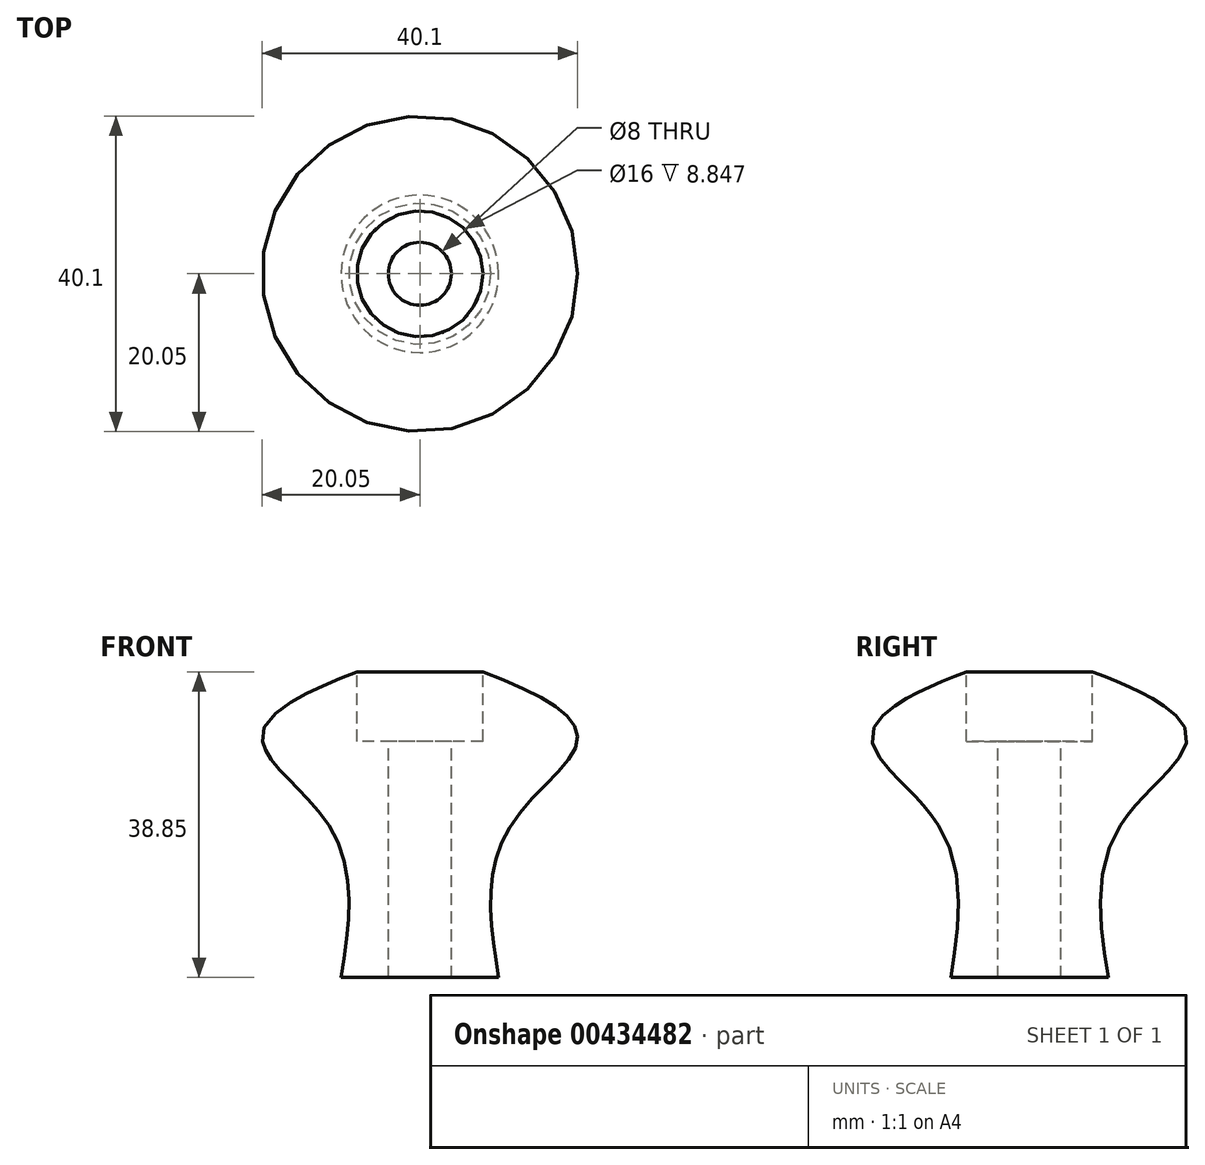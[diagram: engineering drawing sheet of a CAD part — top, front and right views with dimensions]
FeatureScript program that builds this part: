
annotation { "Feature Type Name" : "Feature", "Feature Type Description" : "" }
export const myFeature = defineFeature(function(context is Context, id is Id, definition is map)
    precondition{}
    {
        {
            var Q0;
            Q0=qCreatedBy(makeId("Top.planeOp"),FACE);
            var sketch = newSketch(context, id + "F0", { "sketchPlane" : qUnion([Q0])});
            skCircle(sketch, "E0", {"center": v(0, 0) * mm, "radius": 10 * mm});
            skSolve(sketch);
        }
        {
            var Q0;
            Q0=qCreatedBy(makeId("Top.planeOp"),FACE);
            cPlane(context, id + "F1", {"entities" : qUnion([Q0]), "cplaneType" : CPlaneType.OFFSET, "offset" : 20 * mm, "width" : 150 * mm, "height" : 150 * mm});
        }
        {
            var Q0;
            Q0=qCreatedBy(id+"F1.planeOp",FACE);
            cPlane(context, id + "F2", {"entities" : qUnion([Q0]), "cplaneType" : CPlaneType.OFFSET, "offset" : 10 * mm, "width" : 150 * mm, "height" : 150 * mm});
        }
        {
            var Q0;
            Q0=qCreatedBy(id+"F2.planeOp",FACE);
            cPlane(context, id + "F3", {"entities" : qUnion([Q0]), "cplaneType" : CPlaneType.OFFSET, "offset" : 10 * mm, "width" : 150 * mm, "height" : 150 * mm});
        }
        {
            var Q0;
            Q0=qCreatedBy(id+"F1.planeOp",FACE);
            var sketch = newSketch(context, id + "F4", { "sketchPlane" : qUnion([Q0])});
            skCircle(sketch, "E1", {"center": v(0, 0) * mm, "radius": 12 * mm});
            skSolve(sketch);
        }
        {
            var Q0;
            Q0=qCreatedBy(id+"F2.planeOp",FACE);
            var sketch = newSketch(context, id + "F5", { "sketchPlane" : qUnion([Q0])});
            skCircle(sketch, "E2", {"center": v(0, 0) * mm, "radius": 20 * mm});
            skSolve(sketch);
        }
        {
            var Q0;
            Q0=qCreatedBy(id+"F3.planeOp",FACE);
            var sketch = newSketch(context, id + "F6", { "sketchPlane" : qUnion([Q0])});
            skCircle(sketch, "E3", {"center": v(0, 0) * mm, "radius": 5 * mm});
            skSolve(sketch);
        }
        {
            var Q0;
            Q0=makeQuery(id+"F0.imprint","IMPRINT",FACE,{"disambiguationData":[TD([[makeQuery(id+"F0.imprint","IMPRINT",EDGE,{"derivedFrom":sQuery(id+"F0.wireOp",EDGE,"E0")}),1.0]])]});
            var Q1;
            Q1=makeQuery(id+"F4.imprint","IMPRINT",FACE,{"disambiguationData":[TD([[makeQuery(id+"F4.imprint","IMPRINT",EDGE,{"derivedFrom":sQuery(id+"F4.wireOp",EDGE,"E1")}),1.0]])]});
            var Q2;
            Q2=makeQuery(id+"F5.imprint","IMPRINT",FACE,{"disambiguationData":[TD([[makeQuery(id+"F5.imprint","IMPRINT",EDGE,{"derivedFrom":sQuery(id+"F5.wireOp",EDGE,"E2")}),1.0]])]});
            var Q3;
            Q3=makeQuery(id+"F6.imprint","IMPRINT",FACE,{"disambiguationData":[TD([[makeQuery(id+"F6.imprint","IMPRINT",EDGE,{"derivedFrom":sQuery(id+"F6.wireOp",EDGE,"E3")}),1.0]])]});
            loft(context, id + "F7", {"sheetProfilesArray" : [{ "sheetProfileEntities" : qUnion([Q0]) }, { "sheetProfileEntities" : qUnion([Q1]) }, { "sheetProfileEntities" : qUnion([Q2]) }, { "sheetProfileEntities" : qUnion([Q3]) }]});
        }
        {
            var Q0;
            Q0=qCreatedBy(id+"F3.planeOp",FACE);
            var sketch = newSketch(context, id + "F8", { "sketchPlane" : qUnion([Q0])});
            skCircle(sketch, "E4", {"center": v(0, 0) * mm, "radius": 4 * mm});
            skSolve(sketch);
        }
        {
            var Q0;
            Q0=makeQuery(id+"F8.imprint","IMPRINT",FACE,{"disambiguationData":[TD([[makeQuery(id+"F8.imprint","IMPRINT",EDGE,{"derivedFrom":sQuery(id+"F8.wireOp",EDGE,"E4")}),1.0]])]});
            extrude(context, id + "F9", {"entities" : qUnion([Q0]), "operationType" : NewBodyOperationType.REMOVE, "oppositeDirection" : true, "depth" : 68.6 * mm});
        }
        {
            var Q0;
            Q0=qCreatedBy(id+"F3.planeOp",FACE);
            var sketch = newSketch(context, id + "F10", { "sketchPlane" : qUnion([Q0])});
            skCircle(sketch, "E5", {"center": v(0, 0) * mm, "radius": 8 * mm});
            skSolve(sketch);
        }
        {
            var Q0;
            Q0=makeQuery(id+"F10.imprint","IMPRINT",FACE,{"disambiguationData":[TD([[makeQuery(id+"F10.imprint","IMPRINT",EDGE,{"derivedFrom":sQuery(id+"F10.wireOp",EDGE,"E5")}),1.0]])]});
            extrude(context, id + "F11", {"entities" : qUnion([Q0]), "operationType" : NewBodyOperationType.REMOVE, "oppositeDirection" : true, "depth" : 10 * mm});
        }
    });
